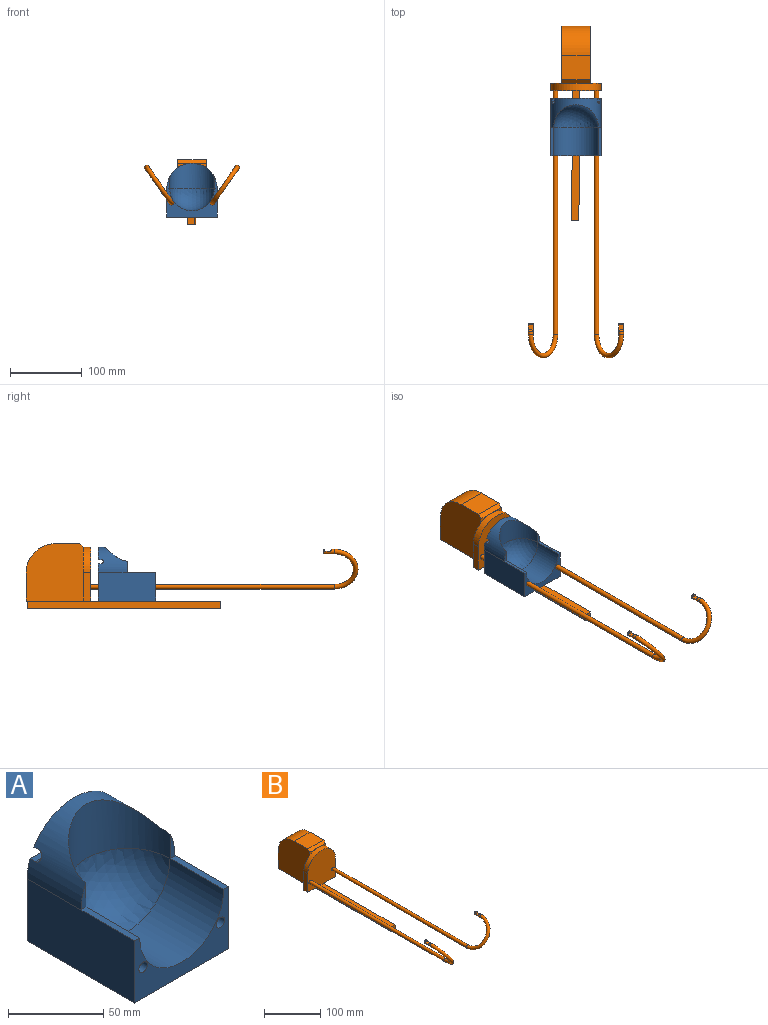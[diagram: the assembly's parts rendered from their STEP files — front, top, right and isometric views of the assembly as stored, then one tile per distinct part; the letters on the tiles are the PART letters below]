
ASSEMBLY  parts=2 mates=1
PART A: 19 faces, bbox 70x80x75 mm
  f0: cylinder r=35mm len=70mm, axis (0,1,0), area 2540.2mm2, adj f1,f2,f3,f4,f5,f10,f14,f16
  f1: plane 60.03x17mm, normal (0,1,0), area 722.2mm2, adj f0,f16
  f2: plane 15.76x3.75mm, normal (0,-1,0), area 39.8mm2, adj f0,f13,f14
  f3: plane 15.76x3.75mm, normal (0,-1,0), area 39.8mm2, adj f0,f12,f14
  f4: plane 80x40mm, normal (1,0,0), area 3200mm2, adj f0,f7,f9,f10,f12
  f5: plane 80x40mm, normal (-1,0,0), area 3200mm2, adj f0,f7,f9,f10,f13
  f6: cylinder r=3.2mm len=80mm, axis (0,1,0), area 1608.5mm2, adj f9,f10
  f7: plane 80x70mm, normal (0,0,-1), area 5600mm2, adj f4,f5,f9,f10
  f8: cylinder r=3.2mm len=80mm, axis (0,1,0), area 1608.5mm2, adj f9,f10
  f9: plane 70x40mm, normal (0,-1,0), area 1201.7mm2, adj f4,f5,f6,f7,f8,f11,f12,f13
  f10: plane 70x52mm, normal (0,1,0), area 3558.9mm2, adj f0,f4,f5,f6,f7,f8,f18
  f11: cylinder r=31.25mm len=62.5mm, axis (0,-1,0), area 3927mm2, adj f9,f12,f13,f15
  f12: plane 40x3.75mm, normal (0,0,1), area 150mm2, adj f3,f4,f9,f11
  f13: plane 40x3.75mm, normal (0,0,1), area 150mm2, adj f2,f5,f9,f11
  f14: cylinder r=31.25mm len=62.5mm, axis (0,0,-1), area 2582.1mm2, adj f0,f2,f3,f15
  f15: sphere r=31.25mm, area 3068mm2, adj f11,f14
  f16: plane 60.03x4mm, normal (0,0,-1), area 240.1mm2, adj f0,f1,f17
  f17: cylinder r=3mm len=65.76mm, axis (1,0,0), area 594.4mm2, adj f0,f16,f18
  f18: plane 65.76x4mm, normal (0,0,1), area 263mm2, adj f0,f10,f17
PART B: 35 faces, bbox 133.1x465.9x90 mm
  f0: plane 20x6.28mm, normal (0,-1,0), area 40.2mm2, adj f4,f29,f33
  f1: plane 68.72x15mm, normal (0,1,0), area 902.3mm2, adj f2,f4,f5,f30
  f2: plane 90x70mm, normal (0,0,-1), area 3014.4mm2, adj f1,f3,f5,f6,f7,f8,f9,f10
  f3: plane 40x10mm, normal (1,0,0), area 400mm2, adj f2,f4,f6,f7
  f4: cylinder r=35mm len=70mm, axis (0,1,0), area 1099.6mm2, adj f0,f1,f3,f5,f6,f7,f28
  f5: plane 40x10mm, normal (-1,0,0), area 400mm2, adj f1,f2,f4,f6
  f6: plane 75x70mm, normal (0,-1,0), area 4659.9mm2, adj f2,f3,f4,f5,f13,f14,f15
  f7: plane 68.72x15mm, normal (0,1,0), area 902.3mm2, adj f2,f3,f4,f29
  f8: plane 270x10mm, normal (-1,0,0), area 2700.1mm2, adj f2,f9,f11,f12,f13
  f9: plane 10x10mm, normal (0,1,0), area 100mm2, adj f2,f8,f10,f12
  f10: plane 270x10mm, normal (1,0,0), area 2700mm2, adj f2,f9,f11,f12,f13
  f11: plane 10x10mm, normal (0,-1,0), area 100mm2, adj f8,f10,f12,f13
  f12: plane 270x11.29mm, normal (0,0,-1), area 2700mm2, adj f8,f9,f10,f11
  f13: plane 181.45x10.87mm, normal (0,0,1), area 1814.4mm2, adj f6,f8,f10,f11
  f14: cylinder r=3.2mm len=340mm, axis (0,1,0), area 6836.1mm2, adj f6,f16
  f15: cylinder r=3.2mm len=340mm, axis (0,1,0), area 6836.1mm2, adj f6,f17
  f16: torus R=30mm, axis (-0.82,0,-0.57), area 1895mm2, adj f14,f20
  f17: torus R=30mm, axis (-0.82,0,0.57), area 1895mm2, adj f15,f18
  f18: cylinder r=3.2mm len=15mm, axis (0,-1,0), area 218.9mm2, adj f17,f19,f25,f26,f27
  f19: plane 6.4x6.4mm, normal (0,1,0), area 32.2mm2, adj f18
  f20: cylinder r=3.2mm len=15mm, axis (0,-1,0), area 218.9mm2, adj f16,f21,f22,f23,f24
  f21: plane 6.4x6.4mm, normal (0,1,0), area 32.2mm2, adj f20
  f22: plane 6.39x6mm, normal (0,0,1), area 38.3mm2, adj f20,f23,f24
  f23: plane 6.39x3mm, normal (0,-1,0), area 14.8mm2, adj f20,f22
  f24: cylinder r=3mm len=6.39mm, axis (-1,0,0), area 25.4mm2, adj f20,f22
  f25: cylinder r=3mm len=6.39mm, axis (-1,0,0), area 25.5mm2, adj f18,f27
  f26: plane 6.39x3mm, normal (0,-1,0), area 14.8mm2, adj f18,f27
  f27: plane 6.39x6mm, normal (0,0,1), area 38.3mm2, adj f18,f25,f26
  f28: plane 20x6.28mm, normal (0,-1,0), area 40.2mm2, adj f4,f30,f33
  f29: plane 80x80mm, normal (1,0,0), area 6026mm2, adj f0,f2,f7,f31,f32,f33,f34
  f30: plane 80x80mm, normal (-1,0,0), area 6026mm2, adj f1,f2,f28,f31,f32,f33,f34
  f31: plane 40x33.96mm, normal (0,0,1), area 1358.3mm2, adj f29,f30,f33,f34
  f32: plane 40x38.96mm, normal (0,1,0), area 1558.3mm2, adj f2,f29,f30,f34
  f33: plane 40x5mm, normal (0,-0.71,0.71), area 282.8mm2, adj f0,f28,f29,f30,f31
  f34: cylinder r=41.04mm len=41.04mm, axis (-1,0,0), area 2578.7mm2, adj f29,f30,f31,f32
PLACE A t=(0,-21.05,0)mm
PLACE B at identity fixed
MATE slider A.f6 <-> B.f14  axis (0,1,0) through (-28.72,-61.05,-20)mm
